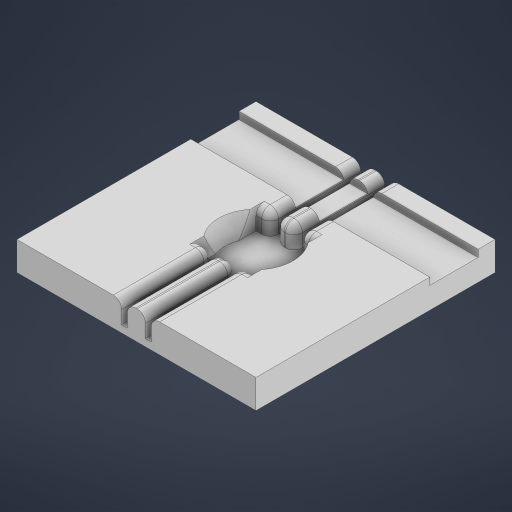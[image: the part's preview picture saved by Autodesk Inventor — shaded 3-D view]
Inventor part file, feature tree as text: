
AUTODESK INVENTOR PART (.ipt)
format: ipt  version: 2023 (Build 270158030, 158C)  size: 312,832 bytes
history: native  units: mm
features: extrude x5, sketch x5, fillet x2, chamfer x2, delete_face x1
ambient origin geometry x8: Origin, YZ Plane, XZ Plane, XY Plane, X Axis, Y Axis, Z Axis, Center Point
bodies: Solid1 (feature_tree)
feature tree (15):
  extrude  "Extrusion1"  Depth=12.1mm
  extrude  "Extrusion2"  Depth=50.0mm
  extrude  "Extrusion3"  Depth=4.5mm
  fillet  "Fillet1"  Radius=3.8mm
  fillet  "Fillet2"  Radius=4.5mm
  extrude  "Extrusion5"  Depth=1.75mm
  chamfer  "Chamfer1"  Distance=13.0mm
  chamfer  "Chamfer2"  Distance=4.5mm
  extrude  "Extrusion6"  Depth=1.5mm
  delete_face  "Delete Face1"
  sketch  "Sketch1"  dims[d0=12.1mm d1=12.1mm]
  sketch  "Sketch2"  dims[d2=50.0mm d3=50.0mm]
  sketch  "Sketch3"  dims[d4=4.5mm d5=0.0mm d6=6.2mm d7=3.8mm d8=4.5mm d9=0.0mm]
  sketch  "Sketch5"  dims[d10=1.5mm d11=0.0mm d15=1.75mm]
  sketch  "Sketch6"  dims[d16=1.75mm d17=13.0mm d18=4.5mm d19=0.0mm d20=1.25mm d21=2.0mm d22=12.997467mm d23=1.25mm d24=2.0mm d25=12.997467mm d26=10.1mm d27=1.5mm d28=0.0mm]
